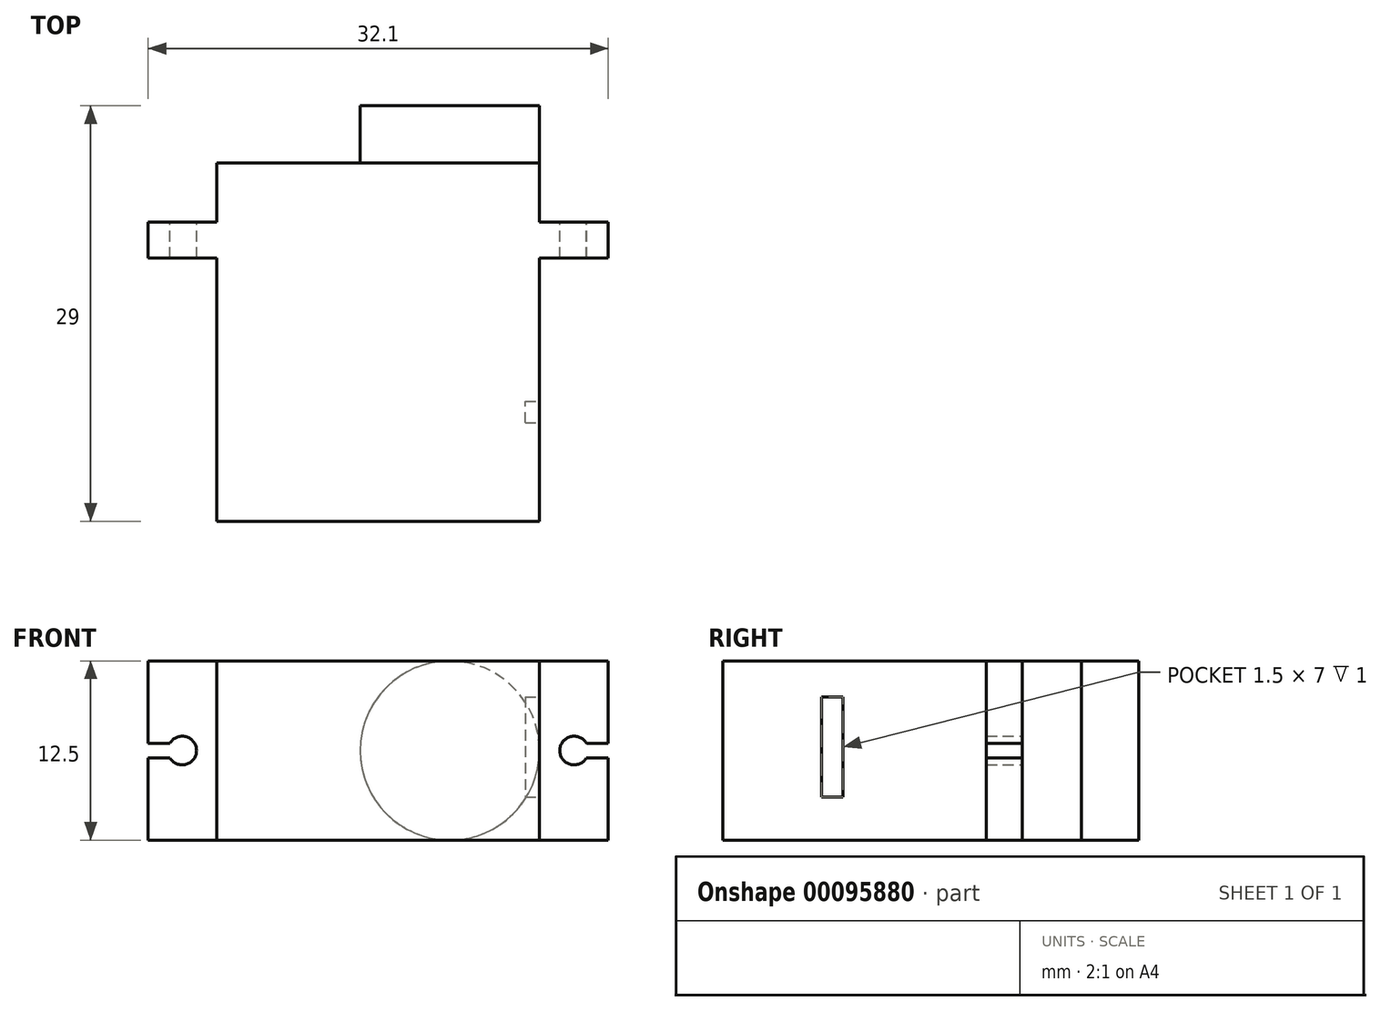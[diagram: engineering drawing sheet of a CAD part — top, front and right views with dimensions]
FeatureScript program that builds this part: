
annotation { "Feature Type Name" : "Feature", "Feature Type Description" : "" }
export const myFeature = defineFeature(function(context is Context, id is Id, definition is map)
    precondition{}
    {
        {
            var Q0;
            Q0=qCreatedBy(makeId("Top.planeOp"),FACE);
            var sketch = newSketch(context, id + "F0", { "sketchPlane" : qUnion([Q0])});
            skLineSegment(sketch, "E0.bottom", {"start": v(3.09, 7.4) * mm, "end": v(25.59, 7.4) * mm});
            skLineSegment(sketch, "E0.top", {"start": v(3.09, -17.6) * mm, "end": v(25.59, -17.6) * mm});
            skLineSegment(sketch, "E0.left", {"start": v(3.09, 7.4) * mm, "end": v(3.09, -17.6) * mm});
            skLineSegment(sketch, "E0.right", {"start": v(25.59, 7.4) * mm, "end": v(25.59, -17.6) * mm});
            skLineSegment(sketch, "E1.bottom", {"start": v(25.59, 3.3) * mm, "end": v(30.39, 3.3) * mm});
            skLineSegment(sketch, "E1.top", {"start": v(25.59, 0.77) * mm, "end": v(30.39, 0.77) * mm});
            skLineSegment(sketch, "E1.left", {"start": v(25.59, 3.3) * mm, "end": v(25.59, 0.77) * mm});
            skLineSegment(sketch, "E1.right", {"start": v(30.39, 3.3) * mm, "end": v(30.39, 0.77) * mm});
            skLineSegment(sketch, "E2.bottom", {"start": v(3.09, 3.3) * mm, "end": v(-1.71, 3.3) * mm});
            skLineSegment(sketch, "E2.top", {"start": v(3.09, 0.77) * mm, "end": v(-1.71, 0.77) * mm});
            skLineSegment(sketch, "E2.left", {"start": v(3.09, 3.3) * mm, "end": v(3.09, 0.77) * mm});
            skLineSegment(sketch, "E2.right", {"start": v(-1.71, 3.3) * mm, "end": v(-1.71, 0.77) * mm});
            skSolve(sketch);
        }
        {
            var Q0;
            {var subQ3=sQuery(id+"F0.wireOp",EDGE,"E0.bottom");Q0=makeQuery(id+"F0.imprint","IMPRINT",FACE,{"disambiguationData":[TD([[makeQuery(id+"F0.imprint","IMPRINT",EDGE,{"derivedFrom":subQ3}),-1.0]])]});}
            var Q1;
            Q1=makeQuery(id+"F0.imprint","IMPRINT",FACE,{"disambiguationData":[TD([[makeQuery(id+"F0.imprint","IMPRINT",EDGE,{"derivedFrom":sQuery(id+"F0.wireOp",EDGE,"E1.bottom")}),-1.0]])]});
            var Q2;
            Q2=makeQuery(id+"F0.imprint","IMPRINT",FACE,{"disambiguationData":[TD([[makeQuery(id+"F0.imprint","IMPRINT",EDGE,{"derivedFrom":sQuery(id+"F0.wireOp",EDGE,"E2.bottom")}),1.0]])]});
            extrude(context, id + "F1", {"entities" : qUnion([Q0, Q1, Q2]), "depth" : 12.5 * mm});
        }
        {
            var Q0;
            {var subQ0=sQuery(id+"F0.wireOp",EDGE,"E0.right");Q0=makeQuery(id+"F1.opExtrude","SWEPT_FACE",FACE,{"disambiguationData":[OSD([subQ0]),TDD([makeQuery(id+"F0.imprint","IMPRINT",EDGE,{"disambiguationData":[TD([[makeQuery(id+"F0.imprint","INTERSECT",VERTEX,{"derivedFrom":[sQuery(id+"F0.wireOp",EDGE,"E0.top"),subQ0]}),1.0]])],"derivedFrom":subQ0})])]});}
            var sketch = newSketch(context, id + "F2", { "sketchPlane" : qUnion([Q0])});
            skLineSegment(sketch, "E3.bottom", {"start": v(-10.73, 3) * mm, "end": v(-9.23, 3) * mm});
            skLineSegment(sketch, "E3.top", {"start": v(-10.73, 10) * mm, "end": v(-9.23, 10) * mm});
            skLineSegment(sketch, "E3.left", {"start": v(-10.73, 10) * mm, "end": v(-10.73, 3) * mm});
            skLineSegment(sketch, "E3.right", {"start": v(-9.23, 10) * mm, "end": v(-9.23, 3) * mm});
            skSolve(sketch);
        }
        {
            var Q0;
            Q0 = qSketchRegion(id + "F2", true);
            extrude(context, id + "F3", {"entities" : qUnion([Q0]), "operationType" : NewBodyOperationType.REMOVE, "oppositeDirection" : true, "depth" : 1 * mm});
        }
        {
            var Q0;
            Q0=makeQuery(id+"F1.opExtrude","SWEPT_FACE",FACE,{"disambiguationData":[OSD([sQuery(id+"F0.wireOp",EDGE,"E0.bottom")])]});
            var sketch = newSketch(context, id + "F4", { "sketchPlane" : qUnion([Q0])});
            skCircle(sketch, "E4", {"center": v(-19.34, 6.25) * mm, "radius": 6.25 * mm});
            skSolve(sketch);
        }
        {
            var Q0;
            Q0 = qSketchRegion(id + "F4", true);
            extrude(context, id + "F5", {"entities" : qUnion([Q0]), "operationType" : NewBodyOperationType.ADD, "depth" : 4 * mm});
        }
        {
            var Q0;
            Q0=makeQuery(id+"F1.opExtrude","SWEPT_FACE",FACE,{"disambiguationData":[OSD([sQuery(id+"F0.wireOp",EDGE,"E1.bottom")])]});
            var sketch = newSketch(context, id + "F6", { "sketchPlane" : qUnion([Q0])});
            skCircle(sketch, "E5", {"center": v(-28, 6.25) * mm, "radius": 1 * mm});
            skLineSegment(sketch, "E6.bottom", {"start": v(-30.39, 6.75) * mm, "end": v(-28.87, 6.75) * mm});
            skLineSegment(sketch, "E6.top", {"start": v(-30.39, 5.75) * mm, "end": v(-28.87, 5.75) * mm});
            skLineSegment(sketch, "E6.left", {"start": v(-30.39, 6.75) * mm, "end": v(-30.39, 5.75) * mm});
            skLineSegment(sketch, "E6.right", {"start": v(-28.87, 6.75) * mm, "end": v(-28.87, 5.75) * mm});
            skSolve(sketch);
        }
        {
            var Q0;
            {var subQ0=sQuery(id+"F6.wireOp",EDGE,"E6.top");Q0=makeQuery(id+"F6.imprint","IMPRINT",FACE,{"disambiguationData":[TD([[makeQuery(id+"F6.imprint","IMPRINT",EDGE,{"derivedFrom":subQ0}),1.0]])]});}
            var Q1;
            {var subQ0=sQuery(id+"F6.wireOp",EDGE,"E6.right");Q1=makeQuery(id+"F6.imprint","IMPRINT",FACE,{"disambiguationData":[TD([[makeQuery(id+"F6.imprint","IMPRINT",EDGE,{"derivedFrom":subQ0}),1.0]])]});}
            var Q2;
            {var subQ0=sQuery(id+"F6.wireOp",EDGE,"E6.right");Q2=makeQuery(id+"F6.imprint","IMPRINT",FACE,{"disambiguationData":[TD([[makeQuery(id+"F6.imprint","IMPRINT",EDGE,{"derivedFrom":subQ0}),-1.0]])]});}
            var Q3;
            Q3=makeQuery(id+"F1.opExtrude","SWEPT_FACE",FACE,{"disambiguationData":[OSD([sQuery(id+"F0.wireOp",EDGE,"E1.top")])]});
            extrude(context, id + "F7", {"entities" : qUnion([Q0, Q1, Q2]), "operationType" : NewBodyOperationType.REMOVE, "endBound" : BoundingType.UP_TO_SURFACE, "oppositeDirection" : true, "endBoundEntityFace" : qUnion([Q3]), "depth" : 25 * mm});
        }
        {
            var Q0;
            Q0=makeQuery(id+"F1.opExtrude","SWEPT_FACE",FACE,{"disambiguationData":[OSD([sQuery(id+"F0.wireOp",EDGE,"E2.bottom")])]});
            var sketch = newSketch(context, id + "F8", { "sketchPlane" : qUnion([Q0])});
            skCircle(sketch, "E7", {"center": v(-0.67, 6.25) * mm, "radius": 1 * mm});
            skLineSegment(sketch, "E8.bottom", {"start": v(1.71, 5.75) * mm, "end": v(-0.29, 5.75) * mm});
            skLineSegment(sketch, "E8.top", {"start": v(1.71, 6.75) * mm, "end": v(-0.29, 6.75) * mm});
            skLineSegment(sketch, "E8.left", {"start": v(1.71, 5.75) * mm, "end": v(1.71, 6.75) * mm});
            skLineSegment(sketch, "E8.right", {"start": v(-0.29, 5.75) * mm, "end": v(-0.29, 6.75) * mm});
            skSolve(sketch);
        }
        {
            var Q0;
            Q0 = qSketchRegion(id + "F8", true);
            var Q1;
            Q1=makeQuery(id+"F1.opExtrude","SWEPT_FACE",FACE,{"disambiguationData":[OSD([sQuery(id+"F0.wireOp",EDGE,"E2.top")])]});
            extrude(context, id + "F9", {"entities" : qUnion([Q0]), "operationType" : NewBodyOperationType.REMOVE, "endBound" : BoundingType.UP_TO_SURFACE, "oppositeDirection" : true, "endBoundEntityFace" : qUnion([Q1]), "depth" : 25 * mm});
        }
    });
